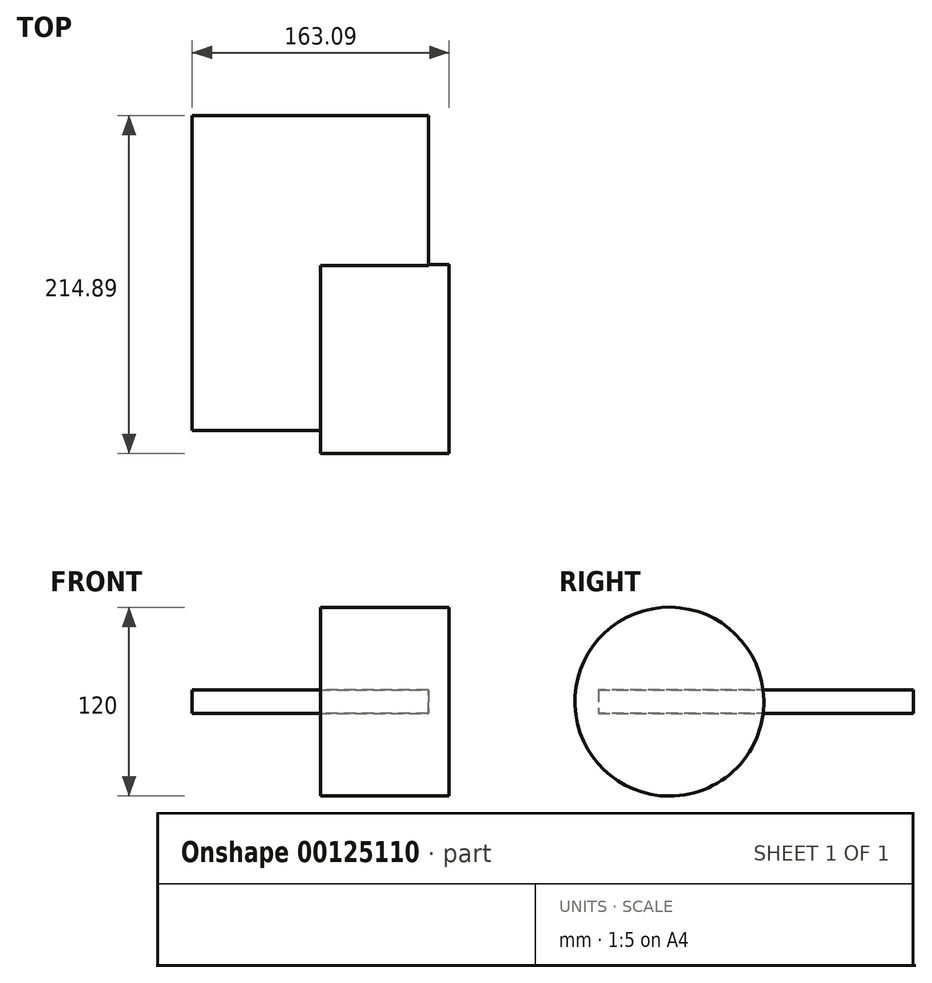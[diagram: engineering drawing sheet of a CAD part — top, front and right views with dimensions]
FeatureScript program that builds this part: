
annotation { "Feature Type Name" : "Feature", "Feature Type Description" : "" }
export const myFeature = defineFeature(function(context is Context, id is Id, definition is map)
    precondition{}
    {
        {
            var Q0;
            Q0=qCreatedBy(makeId("Top.planeOp"),FACE);
            var sketch = newSketch(context, id + "F0", { "sketchPlane" : qUnion([Q0])});
            skLineSegment(sketch, "E0.bottom", {"start": v(-81.64, 150.13) * mm, "end": v(68.36, 150.13) * mm});
            skLineSegment(sketch, "E0.top", {"start": v(-81.64, -49.87) * mm, "end": v(68.36, -49.87) * mm});
            skLineSegment(sketch, "E0.left", {"start": v(-81.64, 150.13) * mm, "end": v(-81.64, -49.87) * mm});
            skLineSegment(sketch, "E0.right", {"start": v(68.36, 150.13) * mm, "end": v(68.36, -49.87) * mm});
            skSolve(sketch);
        }
        {
            var Q0;
            Q0=makeQuery(id+"F0.imprint","IMPRINT",FACE,{"disambiguationData":[TD([[makeQuery(id+"F0.imprint","IMPRINT",EDGE,{"derivedFrom":sQuery(id+"F0.wireOp",EDGE,"E0.bottom")}),-1.0]])]});
            extrude(context, id + "F1", {"entities" : qUnion([Q0]), "depth" : 15 * mm});
        }
        {
            var Q0;
            Q0=qCreatedBy(makeId("Right.planeOp"),FACE);
            var sketch = newSketch(context, id + "F2", { "sketchPlane" : qUnion([Q0])});
            skCircle(sketch, "E1", {"center": v(-4.76, 7.58) * mm, "radius": 60 * mm});
            skSolve(sketch);
        }
        {
            var Q0;
            Q0 = qSketchRegion(id + "F2", true);
            extrude(context, id + "F3", {"entities" : qUnion([Q0]), "operationType" : NewBodyOperationType.ADD, "depth" : 81.45 * mm});
        }
    });
